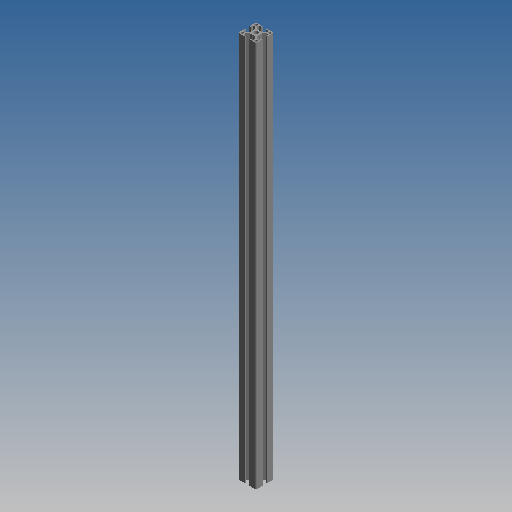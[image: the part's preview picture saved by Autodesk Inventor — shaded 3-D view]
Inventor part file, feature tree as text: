
AUTODESK INVENTOR PART (.ipt)
format: ipt  version: 2020 (Build 240168000, 168)  size: 211,968 bytes
history: native  units: mm (DEFAULTED — no unit token found)
features: other x21, sketch x3, hole x2, extrude x1, pattern_linear x1
ambient origin geometry x8: Origin, YZ Plane, XZ Plane, XY Plane, X Axis, Y Axis, Z Axis, Center Point
bodies: Solid1 (feature_tree)
feature tree (28):
  extrude  "Extrusion1"  Depth=650.0mm
  hole  "Hole1"  [1 undecoded]
  hole  "Hole2"  [1 undecoded]
  pattern_linear  "Rectangular Pattern1"  [2 undecoded]
  other  "C1_XY"
  other  "C1_YZ"
  other  "C1_ZX"
  other  "C1_X"
  other  "C1_Y"
  other  "C1_Z"
  other  "C1_Center"
  other  "to_frame_cap1_XY"
  other  "to_frame_cap1_YZ"
  other  "to_frame_cap1_ZX"
  other  "to_frame_cap1_X"
  other  "to_frame_cap1_Y"
  other  "to_frame_cap1_Z"
  other  "to_frame_cap1_Center"
  other  "to_frame_cap2_XY"
  other  "to_frame_cap2_YZ"
  other  "to_frame_cap2_ZX"
  other  "to_frame_cap2_X"
  other  "to_frame_cap2_Y"
  other  "to_frame_cap2_Z"
  other  "to_frame_cap2_Center"
  sketch  "Sketch_1"  dims[d0=650.0mm d1=0.0mm]
  sketch  "Sketch2"  dims[d2=6.8mm d3=6.0mm d4=4.0mm d5=2.0mm d6=90.0deg d7=650.0mm d8=0.0mm]
  sketch  "Sketch3"  dims[d9=4.2mm d10=6.0mm d11=4.0mm d12=2.0mm d13=90.0deg d14=650.0mm d15=0.0mm d16=20.0mm d18=23.2mm d19=20.0mm d21=23.2mm d22=0.0mm d23=0.0mm d24=0.0mm]
note: 4 required parameter values undecoded (feature->parameter linkage not recoverable at this tier; creation-order binding heuristic only, values carry confidence <= 0.55)
